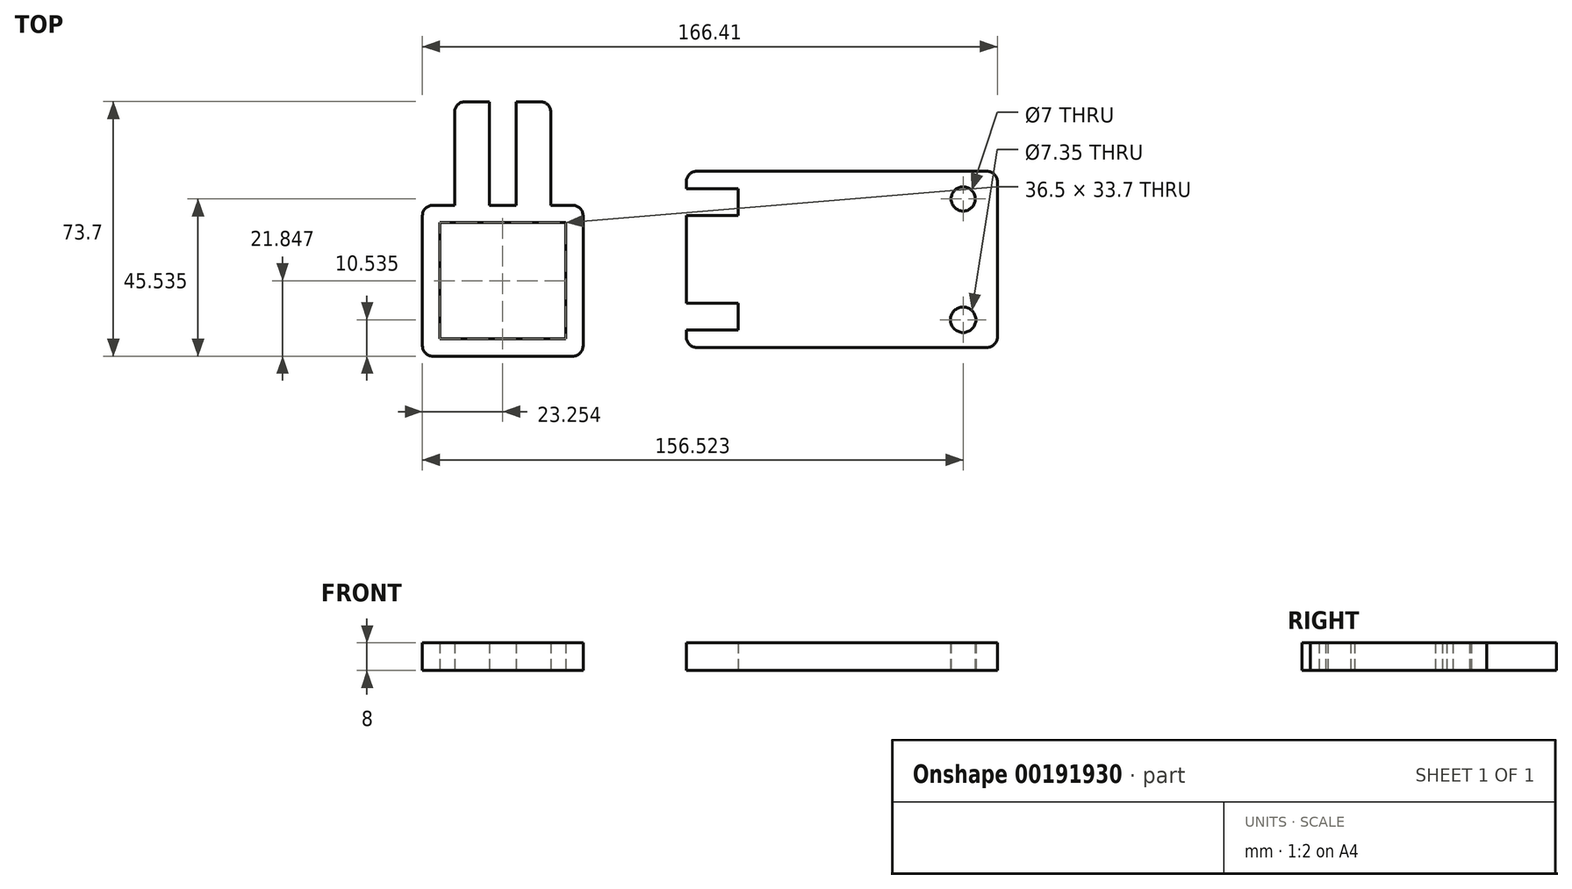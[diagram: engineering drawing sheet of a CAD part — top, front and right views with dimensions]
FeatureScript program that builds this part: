
annotation { "Feature Type Name" : "Feature", "Feature Type Description" : "" }
export const myFeature = defineFeature(function(context is Context, id is Id, definition is map)
    precondition{}
    {
        {
            var Q0;
            Q0=qCreatedBy(makeId("Top.planeOp"),FACE);
            var sketch = newSketch(context, id + "F0", { "sketchPlane" : qUnion([Q0])});
            skLineSegment(sketch, "E0", {"start": v(-56.6, -13.39) * mm, "end": v(33.4, -13.39) * mm});
            skLineSegment(sketch, "E1", {"start": v(33.4, -13.39) * mm, "end": v(33.4, 37.61) * mm});
            skLineSegment(sketch, "E2", {"start": v(33.4, 37.61) * mm, "end": v(-56.6, 37.61) * mm});
            skLineSegment(sketch, "E3", {"start": v(-56.6, 37.61) * mm, "end": v(-56.6, -13.39) * mm});
            skLineSegment(sketch, "E4", {"start": v(-56.6, 32.61) * mm, "end": v(-41.6, 32.61) * mm});
            skLineSegment(sketch, "E5", {"start": v(-41.6, 32.61) * mm, "end": v(-41.6, 24.81) * mm});
            skLineSegment(sketch, "E6", {"start": v(-41.6, 24.81) * mm, "end": v(-56.6, 24.81) * mm});
            skLineSegment(sketch, "E7", {"start": v(-56.6, -0.59) * mm, "end": v(-41.6, -0.59) * mm});
            skLineSegment(sketch, "E8", {"start": v(-41.6, -0.59) * mm, "end": v(-41.6, -8.39) * mm});
            skLineSegment(sketch, "E9", {"start": v(-41.6, -8.39) * mm, "end": v(-56.6, -8.39) * mm});
            skCircle(sketch, "E10", {"center": v(23.5, 29.61) * mm, "radius": 3.5 * mm});
            skCircle(sketch, "E11", {"center": v(23.5, -5.39) * mm, "radius": 3.67 * mm});
            skLineSegment(sketch, "E12", {"start": v(-133.02, -15.92) * mm, "end": v(-86.52, -15.92) * mm});
            skLineSegment(sketch, "E13", {"start": v(-86.52, -15.92) * mm, "end": v(-86.52, 27.78) * mm});
            skLineSegment(sketch, "E14", {"start": v(-86.52, 27.78) * mm, "end": v(-133.02, 27.78) * mm});
            skLineSegment(sketch, "E15", {"start": v(-133.02, 27.78) * mm, "end": v(-133.02, -15.92) * mm});
            skLineSegment(sketch, "E16.0", {"start": v(-91.52, 22.78) * mm, "end": v(-128.02, 22.78) * mm});
            skLineSegment(sketch, "E16.1", {"start": v(-91.52, -10.92) * mm, "end": v(-91.52, 22.78) * mm});
            skLineSegment(sketch, "E16.2", {"start": v(-128.02, -10.92) * mm, "end": v(-91.52, -10.92) * mm});
            skLineSegment(sketch, "E16.3", {"start": v(-128.02, 22.78) * mm, "end": v(-128.02, -10.92) * mm});
            skLineSegment(sketch, "E17", {"start": v(-123.67, 27.78) * mm, "end": v(-123.67, 57.78) * mm});
            skLineSegment(sketch, "E18", {"start": v(-123.67, 57.78) * mm, "end": v(-113.67, 57.78) * mm});
            skLineSegment(sketch, "E19", {"start": v(-113.67, 57.78) * mm, "end": v(-113.67, 27.78) * mm});
            skLineSegment(sketch, "E20", {"start": v(-113.67, 27.78) * mm, "end": v(-105.87, 27.78) * mm});
            skLineSegment(sketch, "E21", {"start": v(-105.87, 27.78) * mm, "end": v(-105.87, 57.78) * mm});
            skLineSegment(sketch, "E22", {"start": v(-105.87, 57.78) * mm, "end": v(-95.87, 57.78) * mm});
            skLineSegment(sketch, "E23", {"start": v(-95.87, 57.78) * mm, "end": v(-95.87, 27.78) * mm});
            skLineSegment(sketch, "E24", {"start": v(-113.67, 42.78) * mm, "end": v(-105.87, 42.78) * mm});
            skSolve(sketch);
        }
        {
            var Q0;
            {var subQ2=sQuery(id+"F0.wireOp",EDGE,"E0");Q0=makeQuery(id+"F0.imprint","IMPRINT",FACE,{"disambiguationData":[TD([[makeQuery(id+"F0.imprint","IMPRINT",EDGE,{"derivedFrom":subQ2}),1.0]])]});}
            extrude(context, id + "F1", {"entities" : qUnion([Q0]), "depth" : 8 * mm});
        }
        {
            var Q0;
            {var subQ3=sQuery(id+"F0.wireOp",EDGE,"E17");Q0=makeQuery(id+"F0.imprint","IMPRINT",FACE,{"disambiguationData":[TD([[makeQuery(id+"F0.imprint","IMPRINT",EDGE,{"derivedFrom":subQ3}),-1.0]])]});}
            var Q1;
            {var subQ0=sQuery(id+"F0.wireOp",EDGE,"E20");Q1=makeQuery(id+"F0.imprint","IMPRINT",FACE,{"disambiguationData":[TD([[makeQuery(id+"F0.imprint","IMPRINT",EDGE,{"derivedFrom":subQ0}),1.0]])]});}
            var Q2;
            {var subQ0=sQuery(id+"F0.wireOp",EDGE,"E22");Q2=makeQuery(id+"F0.imprint","IMPRINT",FACE,{"disambiguationData":[TD([[makeQuery(id+"F0.imprint","IMPRINT",EDGE,{"derivedFrom":subQ0}),-1.0]])]});}
            var Q3;
            Q3=makeQuery(id+"F0.imprint","IMPRINT",FACE,{"disambiguationData":[TD([[makeQuery(id+"F0.imprint","IMPRINT",EDGE,{"derivedFrom":sQuery(id+"F0.wireOp",EDGE,"E12")}),1.0]])]});
            extrude(context, id + "F2", {"entities" : qUnion([Q0, Q1, Q2, Q3]), "operationType" : NewBodyOperationType.ADD, "depth" : 8 * mm});
        }
        {
            var Q0;
            Q0=makeQuery(id+"F2.opExtrude","SWEPT_EDGE",EDGE,{"disambiguationData":[OSD([sQuery(id+"F0.wireOp",EDGE,"E12"),sQuery(id+"F0.wireOp",EDGE,"E15")])]});
            var Q1;
            Q1=makeQuery(id+"F2.opExtrude","SWEPT_EDGE",EDGE,{"disambiguationData":[OSD([sQuery(id+"F0.wireOp",EDGE,"E12"),sQuery(id+"F0.wireOp",EDGE,"E13")])]});
            var Q2;
            Q2=makeQuery(id+"F2.opExtrude","SWEPT_EDGE",EDGE,{"disambiguationData":[OSD([sQuery(id+"F0.wireOp",EDGE,"E13"),sQuery(id+"F0.wireOp",EDGE,"E14")])]});
            var Q3;
            Q3=makeQuery(id+"F2.opExtrude","SWEPT_EDGE",EDGE,{"disambiguationData":[OSD([sQuery(id+"F0.wireOp",EDGE,"E14"),sQuery(id+"F0.wireOp",EDGE,"E15")])]});
            var Q4;
            Q4=makeQuery(id+"F2.opExtrude","SWEPT_EDGE",EDGE,{"disambiguationData":[OSD([sQuery(id+"F0.wireOp",EDGE,"E22"),sQuery(id+"F0.wireOp",EDGE,"E23")])]});
            var Q5;
            Q5=makeQuery(id+"F2.opExtrude","SWEPT_EDGE",EDGE,{"disambiguationData":[OSD([sQuery(id+"F0.wireOp",EDGE,"E17"),sQuery(id+"F0.wireOp",EDGE,"E18")])]});
            var Q6;
            Q6=makeQuery(id+"F1.opExtrude","SWEPT_EDGE",EDGE,{"disambiguationData":[OSD([sQuery(id+"F0.wireOp",EDGE,"E0"),sQuery(id+"F0.wireOp",EDGE,"E1")])]});
            var Q7;
            Q7=makeQuery(id+"F1.opExtrude","SWEPT_EDGE",EDGE,{"disambiguationData":[OSD([sQuery(id+"F0.wireOp",EDGE,"E1"),sQuery(id+"F0.wireOp",EDGE,"E2")])]});
            var Q8;
            Q8=makeQuery(id+"F1.opExtrude","SWEPT_EDGE",EDGE,{"disambiguationData":[OSD([sQuery(id+"F0.wireOp",EDGE,"E0"),sQuery(id+"F0.wireOp",EDGE,"E3")])]});
            var Q9;
            Q9=makeQuery(id+"F1.opExtrude","SWEPT_EDGE",EDGE,{"disambiguationData":[OSD([sQuery(id+"F0.wireOp",EDGE,"E2"),sQuery(id+"F0.wireOp",EDGE,"E3")])]});
            fillet(context, id + "F3", {"entities" : qUnion([Q0, Q1, Q2, Q3, Q4, Q5, Q6, Q7, Q8, Q9]), "radius" : 3 * mm, "tangentPropagation" : true, "allowEdgeOverflow" : false});
        }
    });
